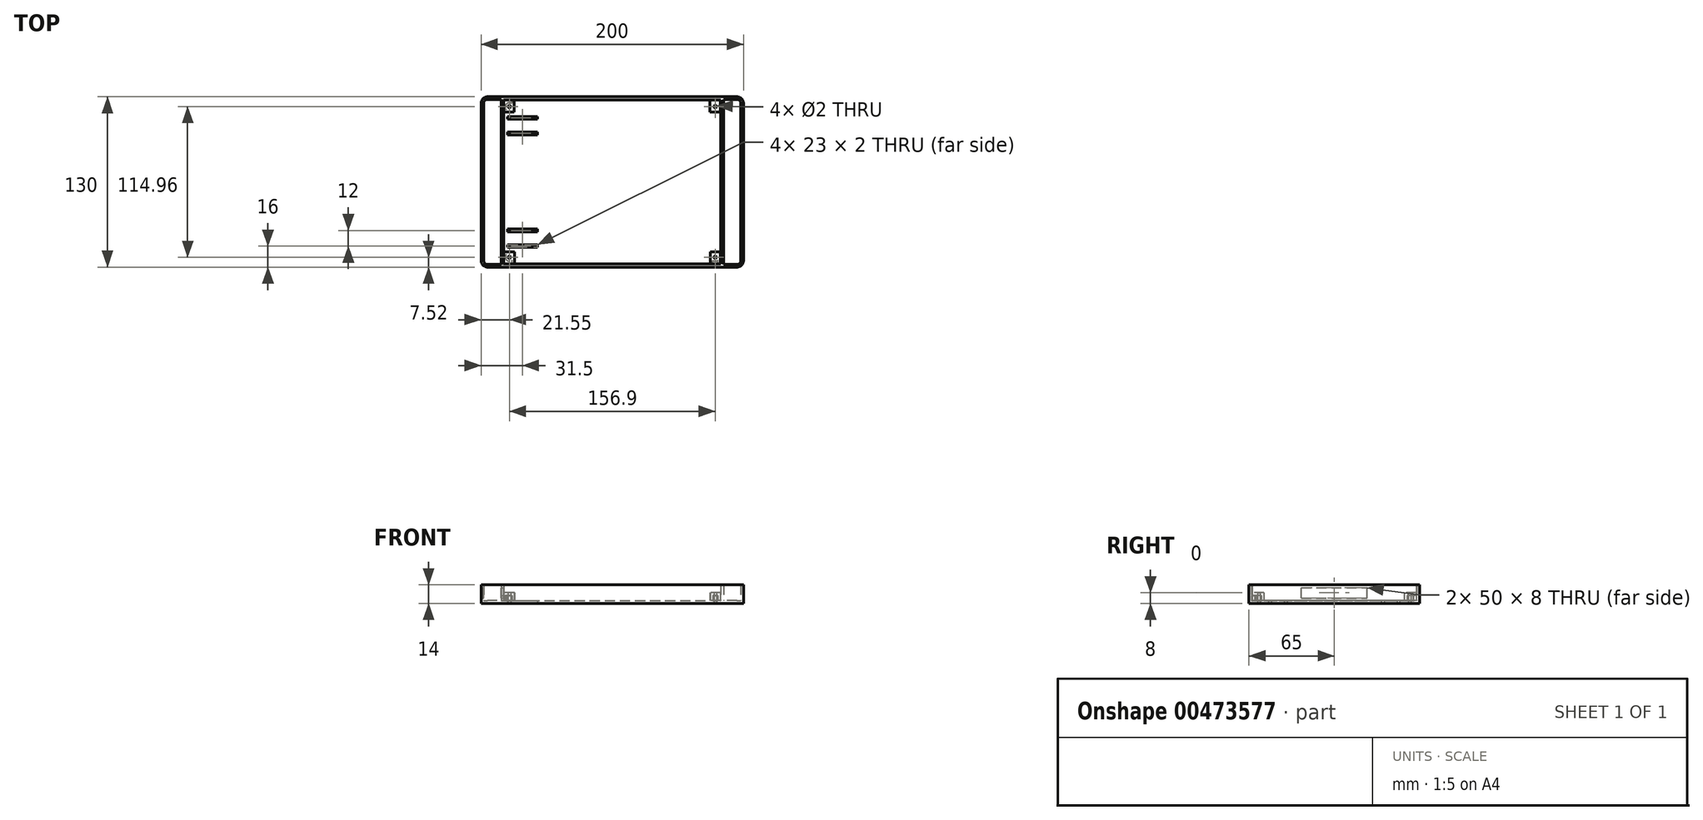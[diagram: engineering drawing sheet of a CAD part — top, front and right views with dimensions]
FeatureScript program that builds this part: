
annotation { "Feature Type Name" : "Feature", "Feature Type Description" : "" }
export const myFeature = defineFeature(function(context is Context, id is Id, definition is map)
    precondition{}
    {
        {
            var Q0;
            Q0=qCreatedBy(makeId("Top.planeOp"),FACE);
            var sketch = newSketch(context, id + "F0", { "sketchPlane" : qUnion([Q0])});
            skLineSegment(sketch, "E0.bottom", {"start": v(79.15, 62.5) * mm, "end": v(77.15, 62.5) * mm});
            skLineSegment(sketch, "E0.top", {"start": v(79.45, -62.5) * mm, "end": v(77.45, -62.5) * mm});
            skLineSegment(sketch, "E0.left", {"start": v(82.75, 59.5) * mm, "end": v(82.75, -58.77) * mm});
            skLineSegment(sketch, "E0.right", {"start": v(-82.75, 59.5) * mm, "end": v(-82.75, -58.77) * mm});
            skPoint(sketch, "E0.middle", {"position": v(0, 0) * mm});
            skLineSegment(sketch, "E1.left", {"start": v(82.45, 53.48) * mm, "end": v(82.45, -53.48) * mm});
            skLineSegment(sketch, "E1.right", {"start": v(-82.45, 53.48) * mm, "end": v(-82.45, -53.48) * mm});
            skPoint(sketch, "E2", {"position": v(-78.45, 57.48) * mm});
            skPoint(sketch, "E3", {"position": v(78.45, 57.48) * mm});
            skPoint(sketch, "E4", {"position": v(78.45, -57.48) * mm});
            skPoint(sketch, "E5", {"position": v(-78.45, -57.48) * mm});
            skPoint(sketch, "E6.visualSharp", {"position": v(-82.75, 62.5) * mm});
            skPoint(sketch, "E7.visualSharp", {"position": v(-82.75, -62.5) * mm});
            skPoint(sketch, "E8.visualSharp", {"position": v(82.75, 62.5) * mm});
            skPoint(sketch, "E9.visualSharp", {"position": v(82.75, -62.5) * mm});
            skLineSegment(sketch, "E10.trimOffspring", {"start": v(-77.45, -62.5) * mm, "end": v(-79.45, -62.5) * mm});
            skLineSegment(sketch, "E11.trimOffspring", {"start": v(-77.75, 62.5) * mm, "end": v(-79.75, 62.5) * mm});
            skPoint(sketch, "E12.visualSharp", {"position": v(74.45, 62.5) * mm});
            skPoint(sketch, "E13.visualSharp", {"position": v(-74.45, -62.5) * mm});
            skPoint(sketch, "E14.visualSharp", {"position": v(74.75, -62.5) * mm});
            skPoint(sketch, "E15.visualSharp", {"position": v(-74.75, 62.5) * mm});
            skLineSegment(sketch, "E16.bottom", {"start": v(82.75, 62.5) * mm, "end": v(-82.75, 62.5) * mm});
            skLineSegment(sketch, "E16.top", {"start": v(82.75, -62.5) * mm, "end": v(-82.75, -62.5) * mm});
            skLineSegment(sketch, "E16.left", {"start": v(82.75, 62.5) * mm, "end": v(82.75, -62.5) * mm});
            skLineSegment(sketch, "E16.right", {"start": v(-82.75, 62.5) * mm, "end": v(-82.75, -62.5) * mm});
            skLineSegment(sketch, "E17.bottom", {"start": v(100, 65) * mm, "end": v(-100, 65) * mm});
            skLineSegment(sketch, "E17.top", {"start": v(100, -65) * mm, "end": v(-100, -65) * mm});
            skLineSegment(sketch, "E17.left", {"start": v(100, 65) * mm, "end": v(100, -65) * mm});
            skLineSegment(sketch, "E17.right", {"start": v(-100, 65) * mm, "end": v(-100, -65) * mm});
            skLineSegment(sketch, "E18.bottom", {"start": v(-82.75, 62.5) * mm, "end": v(-74.75, 62.5) * mm});
            skLineSegment(sketch, "E18.top", {"start": v(-82.75, 53.48) * mm, "end": v(-74.75, 53.48) * mm});
            skLineSegment(sketch, "E18.left", {"start": v(-82.75, 62.5) * mm, "end": v(-82.75, 53.48) * mm});
            skLineSegment(sketch, "E18.right", {"start": v(-74.75, 62.5) * mm, "end": v(-74.75, 53.48) * mm});
            skLineSegment(sketch, "E19.bottom", {"start": v(-82.75, -62.5) * mm, "end": v(-74.45, -62.5) * mm});
            skLineSegment(sketch, "E19.top", {"start": v(-82.75, -53.48) * mm, "end": v(-74.45, -53.48) * mm});
            skLineSegment(sketch, "E19.left", {"start": v(-82.75, -62.5) * mm, "end": v(-82.75, -53.48) * mm});
            skLineSegment(sketch, "E19.right", {"start": v(-74.45, -62.5) * mm, "end": v(-74.45, -53.48) * mm});
            skLineSegment(sketch, "E20.bottom", {"start": v(74.45, 62.5) * mm, "end": v(82.45, 62.5) * mm});
            skLineSegment(sketch, "E20.top", {"start": v(74.45, 53.48) * mm, "end": v(82.45, 53.48) * mm});
            skLineSegment(sketch, "E20.left", {"start": v(74.45, 62.5) * mm, "end": v(74.45, 53.48) * mm});
            skLineSegment(sketch, "E20.right", {"start": v(82.45, 62.5) * mm, "end": v(82.45, 53.48) * mm});
            skLineSegment(sketch, "E21.bottom", {"start": v(74.75, -62.5) * mm, "end": v(82.45, -62.5) * mm});
            skLineSegment(sketch, "E21.top", {"start": v(74.75, -53.48) * mm, "end": v(82.45, -53.48) * mm});
            skLineSegment(sketch, "E21.left", {"start": v(74.75, -62.5) * mm, "end": v(74.75, -53.48) * mm});
            skLineSegment(sketch, "E21.right", {"start": v(82.45, -62.5) * mm, "end": v(82.45, -53.48) * mm});
            skSolve(sketch);
        }
        {
            var Q0;
            Q0=makeQuery(id+"F0.imprint","IMPRINT",FACE,{"disambiguationData":[TD([[makeQuery(id+"F0.imprint","IMPRINT",EDGE,{"derivedFrom":sQuery(id+"F0.wireOp",EDGE,"E17.bottom")}),1.0]])]});
            var Q1;
            Q1=makeQuery(id+"F0.imprint","IMPRINT",FACE,{"disambiguationData":[TD([[makeQuery(id+"F0.imprint","IMPRINT",EDGE,{"derivedFrom":sQuery(id+"F0.wireOp",EDGE,"E1.left")}),-1.0]])]});
            var Q2;
            {var subQ4=sQuery(id+"F0.wireOp",EDGE,"E18.right");Q2=makeQuery(id+"F0.imprint","IMPRINT",FACE,{"disambiguationData":[TD([[makeQuery(id+"F0.imprint","IMPRINT",EDGE,{"derivedFrom":subQ4}),-1.0]])]});}
            var Q3;
            Q3=makeQuery(id+"F0.imprint","IMPRINT",FACE,{"disambiguationData":[TD([[makeQuery(id+"F0.imprint","IMPRINT",EDGE,{"derivedFrom":sQuery(id+"F0.wireOp",EDGE,"E20.top")}),1.0]])]});
            var Q4;
            Q4=makeQuery(id+"F0.imprint","IMPRINT",FACE,{"disambiguationData":[TD([[makeQuery(id+"F0.imprint","IMPRINT",EDGE,{"derivedFrom":sQuery(id+"F0.wireOp",EDGE,"E21.top")}),-1.0]])]});
            var Q5;
            {var subQ4=sQuery(id+"F0.wireOp",EDGE,"E19.right");Q5=makeQuery(id+"F0.imprint","IMPRINT",FACE,{"disambiguationData":[TD([[makeQuery(id+"F0.imprint","IMPRINT",EDGE,{"derivedFrom":subQ4}),1.0]])]});}
            var Q6;
            {var subQ0=sQuery(id+"F0.wireOp",EDGE,"E1.right");Q6=makeQuery(id+"F0.imprint","IMPRINT",FACE,{"disambiguationData":[TD([[makeQuery(id+"F0.imprint","IMPRINT",EDGE,{"derivedFrom":subQ0}),-1.0]])]});}
            var Q7;
            Q7=makeQuery(id+"F0.imprint","IMPRINT",FACE,{"disambiguationData":[TD([[makeQuery(id+"F0.imprint","IMPRINT",EDGE,{"derivedFrom":sQuery(id+"F0.wireOp",EDGE,"E1.left")}),1.0]])]});
            extrude(context, id + "F1", {"entities" : qUnion([Q0, Q1, Q2, Q3, Q4, Q5, Q6, Q7]), "depth" : 2 * mm});
        }
        {
            var Q0;
            Q0=makeQuery(id+"F0.imprint","IMPRINT",FACE,{"disambiguationData":[TD([[makeQuery(id+"F0.imprint","IMPRINT",EDGE,{"derivedFrom":sQuery(id+"F0.wireOp",EDGE,"E17.bottom")}),1.0]])]});
            extrude(context, id + "F2", {"entities" : qUnion([Q0]), "operationType" : NewBodyOperationType.ADD, "depth" : 14 * mm});
        }
        {
            var Q0;
            {var subQ4=sQuery(id+"F0.wireOp",EDGE,"E19.right");Q0=makeQuery(id+"F0.imprint","IMPRINT",FACE,{"disambiguationData":[TD([[makeQuery(id+"F0.imprint","IMPRINT",EDGE,{"derivedFrom":subQ4}),1.0]])]});}
            var Q1;
            {var subQ4=sQuery(id+"F0.wireOp",EDGE,"E18.right");Q1=makeQuery(id+"F0.imprint","IMPRINT",FACE,{"disambiguationData":[TD([[makeQuery(id+"F0.imprint","IMPRINT",EDGE,{"derivedFrom":subQ4}),-1.0]])]});}
            var Q2;
            Q2=makeQuery(id+"F0.imprint","IMPRINT",FACE,{"disambiguationData":[TD([[makeQuery(id+"F0.imprint","IMPRINT",EDGE,{"derivedFrom":sQuery(id+"F0.wireOp",EDGE,"E21.top")}),-1.0]])]});
            var Q3;
            Q3=makeQuery(id+"F0.imprint","IMPRINT",FACE,{"disambiguationData":[TD([[makeQuery(id+"F0.imprint","IMPRINT",EDGE,{"derivedFrom":sQuery(id+"F0.wireOp",EDGE,"E20.top")}),1.0]])]});
            extrude(context, id + "F3", {"entities" : qUnion([Q0, Q1, Q2, Q3]), "operationType" : NewBodyOperationType.ADD, "depth" : 8 * mm});
        }
        {
            var Q0;
            Q0=sQuery(id+"F0.wireOp",VERTEX,"E5");
            var Q1;
            Q1=sQuery(id+"F0.wireOp",VERTEX,"E4");
            var Q2;
            Q2=sQuery(id+"F0.wireOp",VERTEX,"E2");
            var Q3;
            Q3=sQuery(id+"F0.wireOp",VERTEX,"E3");
            var Q4;
            Q4=makeQuery(id+"F1.opExtrude","SWEPT_BODY",BODY,{"disambiguationData":[OSD([sQuery(id+"F0.wireOp",EDGE,"E1.left"),sQuery(id+"F0.wireOp",EDGE,"E1.right"),sQuery(id+"F0.wireOp",EDGE,"E16.bottom"),sQuery(id+"F0.wireOp",EDGE,"E16.top"),sQuery(id+"F0.wireOp",EDGE,"E16.left"),sQuery(id+"F0.wireOp",EDGE,"E16.right"),sQuery(id+"F0.wireOp",EDGE,"E17.bottom"),sQuery(id+"F0.wireOp",EDGE,"E17.top"),sQuery(id+"F0.wireOp",EDGE,"E17.left"),sQuery(id+"F0.wireOp",EDGE,"E17.right"),sQuery(id+"F0.wireOp",EDGE,"E18.top"),sQuery(id+"F0.wireOp",EDGE,"E19.top"),sQuery(id+"F0.wireOp",EDGE,"E20.right"),sQuery(id+"F0.wireOp",EDGE,"E21.right")])]});
            hole(context, id + "F4", {"style" : HoleStyle.SIMPLE, "endStyle" : HoleEndStyle.THROUGH, "oppositeDirection" : true, "holeDiameter" : 2 * mm, "isTappedThrough" : true, "tappedDepth" : 12 * mm, "tapClearance" : 3, "locations" : qUnion([Q0, Q1, Q2, Q3]), "scope" : qUnion([Q4])});
        }
        {
            var Q0;
            {var subQ0=sQuery(id+"F0.wireOp",EDGE,"E17.right");var subQ1=sQuery(id+"F0.wireOp",EDGE,"E17.top");Q0=makeQuery(id+"F2.boolean.opBoolean","MERGE",EDGE,{"derivedFrom":[makeQuery(id+"F1.opExtrude","SWEPT_EDGE",EDGE,{"disambiguationData":[OSD([subQ1,subQ0])]}),makeQuery(id+"F2.opExtrude","SWEPT_EDGE",EDGE,{"disambiguationData":[OSD([subQ1,subQ0])]})]});}
            var Q1;
            {var subQ0=sQuery(id+"F0.wireOp",EDGE,"E17.right");var subQ1=sQuery(id+"F0.wireOp",EDGE,"E17.bottom");Q1=makeQuery(id+"F2.boolean.opBoolean","MERGE",EDGE,{"derivedFrom":[makeQuery(id+"F1.opExtrude","SWEPT_EDGE",EDGE,{"disambiguationData":[OSD([subQ1,subQ0])]}),makeQuery(id+"F2.opExtrude","SWEPT_EDGE",EDGE,{"disambiguationData":[OSD([subQ1,subQ0])]})]});}
            var Q2;
            {var subQ0=sQuery(id+"F0.wireOp",EDGE,"E17.left");var subQ1=sQuery(id+"F0.wireOp",EDGE,"E17.bottom");Q2=makeQuery(id+"F2.boolean.opBoolean","MERGE",EDGE,{"derivedFrom":[makeQuery(id+"F1.opExtrude","SWEPT_EDGE",EDGE,{"disambiguationData":[OSD([subQ1,subQ0])]}),makeQuery(id+"F2.opExtrude","SWEPT_EDGE",EDGE,{"disambiguationData":[OSD([subQ1,subQ0])]})]});}
            var Q3;
            {var subQ0=sQuery(id+"F0.wireOp",EDGE,"E17.left");var subQ1=sQuery(id+"F0.wireOp",EDGE,"E17.top");Q3=makeQuery(id+"F2.boolean.opBoolean","MERGE",EDGE,{"derivedFrom":[makeQuery(id+"F1.opExtrude","SWEPT_EDGE",EDGE,{"disambiguationData":[OSD([subQ1,subQ0])]}),makeQuery(id+"F2.opExtrude","SWEPT_EDGE",EDGE,{"disambiguationData":[OSD([subQ1,subQ0])]})]});}
            fillet(context, id + "F5", {"entities" : qUnion([Q0, Q1, Q2, Q3]), "radius" : 5 * mm, "tangentPropagation" : true, "allowEdgeOverflow" : false});
        }
        {
            var Q0;
            Q0=makeQuery(id+"F2.opExtrude","CAP_FACE",FACE,{"disambiguationData":[OSD([sQuery(id+"F0.wireOp",EDGE,"E16.bottom"),sQuery(id+"F0.wireOp",EDGE,"E16.top"),sQuery(id+"F0.wireOp",EDGE,"E16.left"),sQuery(id+"F0.wireOp",EDGE,"E16.right"),sQuery(id+"F0.wireOp",EDGE,"E17.bottom"),sQuery(id+"F0.wireOp",EDGE,"E17.top"),sQuery(id+"F0.wireOp",EDGE,"E17.left"),sQuery(id+"F0.wireOp",EDGE,"E17.right")])],"isStart":false});
            shell(context, id + "F6", {"entities" : qUnion([Q0]), "thickness" : 2 * mm});
        }
        {
            var Q0;
            Q0=makeQuery(id+"F1.opExtrude","CAP_FACE",FACE,{"disambiguationData":[OSD([sQuery(id+"F0.wireOp",EDGE,"E17.bottom"),sQuery(id+"F0.wireOp",EDGE,"E17.top"),sQuery(id+"F0.wireOp",EDGE,"E17.left"),sQuery(id+"F0.wireOp",EDGE,"E17.right")])],"isStart":true});
            var sketch = newSketch(context, id + "F7", { "sketchPlane" : qUnion([Q0])});
            skLineSegment(sketch, "E22.bottom", {"start": v(20, 50) * mm, "end": v(-20, 50) * mm});
            skLineSegment(sketch, "E22.top", {"start": v(20, -50) * mm, "end": v(-20, -50) * mm});
            skLineSegment(sketch, "E22.left", {"start": v(20, 50) * mm, "end": v(20, -50) * mm});
            skLineSegment(sketch, "E22.right", {"start": v(-20, 50) * mm, "end": v(-20, -50) * mm});
            skPoint(sketch, "E22.middle", {"position": v(0, 0) * mm});
            skLineSegment(sketch, "E23.bottom", {"start": v(20, 48) * mm, "end": v(-20, 48) * mm});
            skLineSegment(sketch, "E23.top", {"start": v(20, -48) * mm, "end": v(-20, -48) * mm});
            skLineSegment(sketch, "E23.left", {"start": v(20, 48) * mm, "end": v(20, -48) * mm});
            skLineSegment(sketch, "E23.right", {"start": v(-20, 48) * mm, "end": v(-20, -48) * mm});
            skLineSegment(sketch, "E24.1.0.0", {"start": v(40, 50) * mm, "end": v(40, -50) * mm});
            skLineSegment(sketch, "E24.1.0.1", {"start": v(80, 48) * mm, "end": v(40, 48) * mm});
            skLineSegment(sketch, "E24.1.0.2", {"start": v(80, -48) * mm, "end": v(40, -48) * mm});
            skLineSegment(sketch, "E24.1.0.3", {"start": v(80, 50) * mm, "end": v(40, 50) * mm});
            skLineSegment(sketch, "E24.1.0.4", {"start": v(80, 50) * mm, "end": v(80, -50) * mm});
            skLineSegment(sketch, "E24.1.0.5", {"start": v(40, 48) * mm, "end": v(40, -48) * mm});
            skLineSegment(sketch, "E24.1.0.6", {"start": v(80, -50) * mm, "end": v(40, -50) * mm});
            skLineSegment(sketch, "E24.1.0.7", {"start": v(80, 48) * mm, "end": v(80, -48) * mm});
            skLineSegment(sketch, "E24.direction1", {"start": v(-20, -48) * mm, "end": v(40, -48) * mm, "construction": true});
            skLineSegment(sketch, "E25.1.0.0", {"start": v(-40, -50) * mm, "end": v(-80, -50) * mm});
            skLineSegment(sketch, "E25.1.0.1", {"start": v(-40, 50) * mm, "end": v(-80, 50) * mm});
            skLineSegment(sketch, "E25.1.0.2", {"start": v(-40, 48) * mm, "end": v(-80, 48) * mm});
            skLineSegment(sketch, "E25.1.0.3", {"start": v(-40, 50) * mm, "end": v(-40, -50) * mm});
            skLineSegment(sketch, "E25.1.0.4", {"start": v(-40, -48) * mm, "end": v(-80, -48) * mm});
            skLineSegment(sketch, "E25.1.0.5", {"start": v(-80, 50) * mm, "end": v(-80, -50) * mm});
            skLineSegment(sketch, "E25.direction1", {"start": v(-20, -50) * mm, "end": v(-80, -50) * mm, "construction": true});
            skLineSegment(sketch, "E26", {"start": v(80, 38) * mm, "end": v(40, 38) * mm});
            skLineSegment(sketch, "E27", {"start": v(80, -38) * mm, "end": v(40, -38) * mm});
            skLineSegment(sketch, "E28", {"start": v(80, 36) * mm, "end": v(40, 36) * mm});
            skLineSegment(sketch, "E29", {"start": v(80, -36) * mm, "end": v(40, -36) * mm});
            skLineSegment(sketch, "E30.trimOffspring", {"start": v(20, 36) * mm, "end": v(-20, 36) * mm});
            skLineSegment(sketch, "E31.trimOffspring", {"start": v(20, 38) * mm, "end": v(-20, 38) * mm});
            skLineSegment(sketch, "E32.trimOffspring", {"start": v(20, -38) * mm, "end": v(-20, -38) * mm});
            skLineSegment(sketch, "E33.trimOffspring", {"start": v(20, -36) * mm, "end": v(-20, -36) * mm});
            skLineSegment(sketch, "E34.trimOffspring", {"start": v(-40, -38) * mm, "end": v(-80, -38) * mm});
            skLineSegment(sketch, "E35.trimOffspring", {"start": v(-40, -36) * mm, "end": v(-80, -36) * mm});
            skLineSegment(sketch, "E36.trimOffspring", {"start": v(-40, 36) * mm, "end": v(-80, 36) * mm});
            skLineSegment(sketch, "E37.trimOffspring", {"start": v(-40, 38) * mm, "end": v(-80, 38) * mm});
            skLineSegment(sketch, "E38", {"start": v(-57, 50) * mm, "end": v(-57, -50) * mm});
            skSolve(sketch);
        }
        {
            var Q0;
            {var subQ0=sQuery(id+"F7.wireOp",EDGE,"E25.1.0.5");var subQ1=sQuery(id+"F7.wireOp",EDGE,"E25.1.0.1");var subQ2=makeQuery(id+"F7.imprint","INTERSECT",VERTEX,{"derivedFrom":[subQ1,subQ0]});Q0=makeQuery(id+"F7.imprint","IMPRINT",FACE,{"disambiguationData":[TD([[makeQuery(id+"F7.imprint","IMPRINT",EDGE,{"disambiguationData":[TD([[subQ2,1.0]])],"derivedFrom":subQ1}),1.0]])]});}
            var Q1;
            {var subQ0=sQuery(id+"F7.wireOp",EDGE,"E36.trimOffspring");var subQ1=sQuery(id+"F7.wireOp",EDGE,"E25.1.0.5");var subQ2=makeQuery(id+"F7.imprint","INTERSECT",VERTEX,{"derivedFrom":[subQ1,subQ0]});Q1=makeQuery(id+"F7.imprint","IMPRINT",FACE,{"disambiguationData":[TD([[makeQuery(id+"F7.imprint","IMPRINT",EDGE,{"disambiguationData":[TD([[subQ2,1.0]])],"derivedFrom":subQ1}),1.0]])]});}
            var Q2;
            {var subQ0=sQuery(id+"F7.wireOp",EDGE,"E34.trimOffspring");var subQ1=sQuery(id+"F7.wireOp",EDGE,"E25.1.0.5");var subQ2=makeQuery(id+"F7.imprint","INTERSECT",VERTEX,{"derivedFrom":[subQ1,subQ0]});Q2=makeQuery(id+"F7.imprint","IMPRINT",FACE,{"disambiguationData":[TD([[makeQuery(id+"F7.imprint","IMPRINT",EDGE,{"disambiguationData":[TD([[subQ2,1.0]])],"derivedFrom":subQ1}),1.0]])]});}
            var Q3;
            {var subQ0=sQuery(id+"F7.wireOp",EDGE,"E25.1.0.5");var subQ1=sQuery(id+"F7.wireOp",EDGE,"E25.1.0.0");var subQ2=makeQuery(id+"F7.imprint","INTERSECT",VERTEX,{"derivedFrom":[subQ1,subQ0]});Q3=makeQuery(id+"F7.imprint","IMPRINT",FACE,{"disambiguationData":[TD([[makeQuery(id+"F7.imprint","IMPRINT",EDGE,{"disambiguationData":[TD([[subQ2,1.0]])],"derivedFrom":subQ1}),-1.0]])]});}
            extrude(context, id + "F8", {"entities" : qUnion([Q0, Q1, Q2, Q3]), "operationType" : NewBodyOperationType.REMOVE, "oppositeDirection" : true, "depth" : 22.5 * mm});
        }
        {
            var Q0;
            Q0=makeQuery(id+"F2.opExtrude","SWEPT_FACE",FACE,{"disambiguationData":[OSD([sQuery(id+"F0.wireOp",EDGE,"E16.right"),sQuery(id+"F0.wireOp",EDGE,"E18.left"),sQuery(id+"F0.wireOp",EDGE,"E19.left")])]});
            var sketch = newSketch(context, id + "F9", { "sketchPlane" : qUnion([Q0])});
            skLineSegment(sketch, "E39.bottom", {"start": v(-25, 2) * mm, "end": v(25, 2) * mm});
            skLineSegment(sketch, "E39.top", {"start": v(-25, 14) * mm, "end": v(25, 14) * mm});
            skLineSegment(sketch, "E39.left", {"start": v(-25, 2) * mm, "end": v(-25, 14) * mm});
            skLineSegment(sketch, "E39.right", {"start": v(25, 2) * mm, "end": v(25, 14) * mm});
            skLineSegment(sketch, "E40.bottom", {"start": v(-25, 12) * mm, "end": v(25, 12) * mm});
            skLineSegment(sketch, "E40.top", {"start": v(-25, 4) * mm, "end": v(25, 4) * mm});
            skLineSegment(sketch, "E40.left", {"start": v(-25, 12) * mm, "end": v(-25, 4) * mm});
            skLineSegment(sketch, "E40.right", {"start": v(25, 12) * mm, "end": v(25, 4) * mm});
            skSolve(sketch);
        }
        {
            var Q0;
            Q0=makeQuery(id+"F9.imprint","IMPRINT",FACE,{"disambiguationData":[TD([[makeQuery(id+"F9.imprint","IMPRINT",EDGE,{"derivedFrom":sQuery(id+"F9.wireOp",EDGE,"E40.bottom")}),-1.0]])]});
            var Q1;
            {var subQ0=sQuery(id+"F9.wireOp",EDGE,"E39.top");Q1=makeQuery(id+"F9.imprint","IMPRINT",FACE,{"disambiguationData":[TD([[makeQuery(id+"F9.imprint","IMPRINT",EDGE,{"derivedFrom":subQ0}),-1.0]])]});}
            extrude(context, id + "F10", {"entities" : qUnion([Q0, Q1]), "operationType" : NewBodyOperationType.REMOVE, "oppositeDirection" : true, "depth" : 25 * mm});
        }
    });
